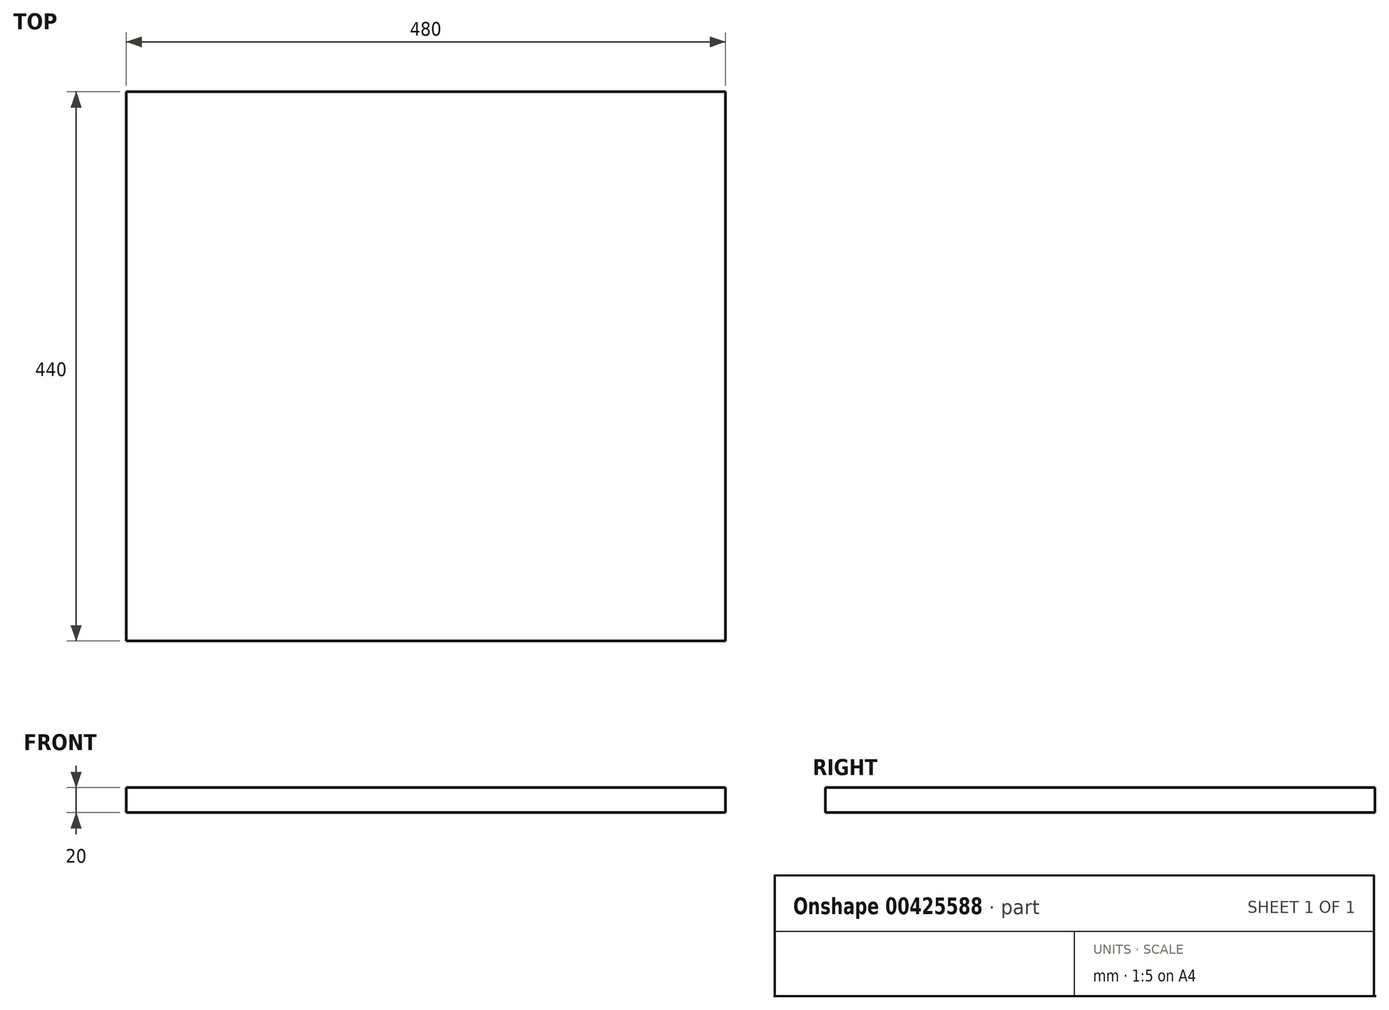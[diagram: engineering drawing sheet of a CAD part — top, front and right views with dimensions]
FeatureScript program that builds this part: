
annotation { "Feature Type Name" : "Feature", "Feature Type Description" : "" }
export const myFeature = defineFeature(function(context is Context, id is Id, definition is map)
    precondition{}
    {
        {
            var Q0;
            Q0=qCreatedBy(makeId("Top.planeOp"),FACE);
            var sketch = newSketch(context, id + "F0", { "sketchPlane" : qUnion([Q0])});
            skLineSegment(sketch, "E0.bottom", {"start": v(-92.28, 376.06) * mm, "end": v(387.72, 376.06) * mm});
            skLineSegment(sketch, "E0.top", {"start": v(-92.28, -63.94) * mm, "end": v(387.72, -63.94) * mm});
            skLineSegment(sketch, "E0.left", {"start": v(-92.28, 376.06) * mm, "end": v(-92.28, -63.94) * mm});
            skLineSegment(sketch, "E0.right", {"start": v(387.72, 376.06) * mm, "end": v(387.72, -63.94) * mm});
            skSolve(sketch);
        }
        {
            var Q0;
            Q0 = qSketchRegion(id + "F0", true);
            extrude(context, id + "F1", {"entities" : qUnion([Q0]), "depth" : 20 * mm});
        }
    });
